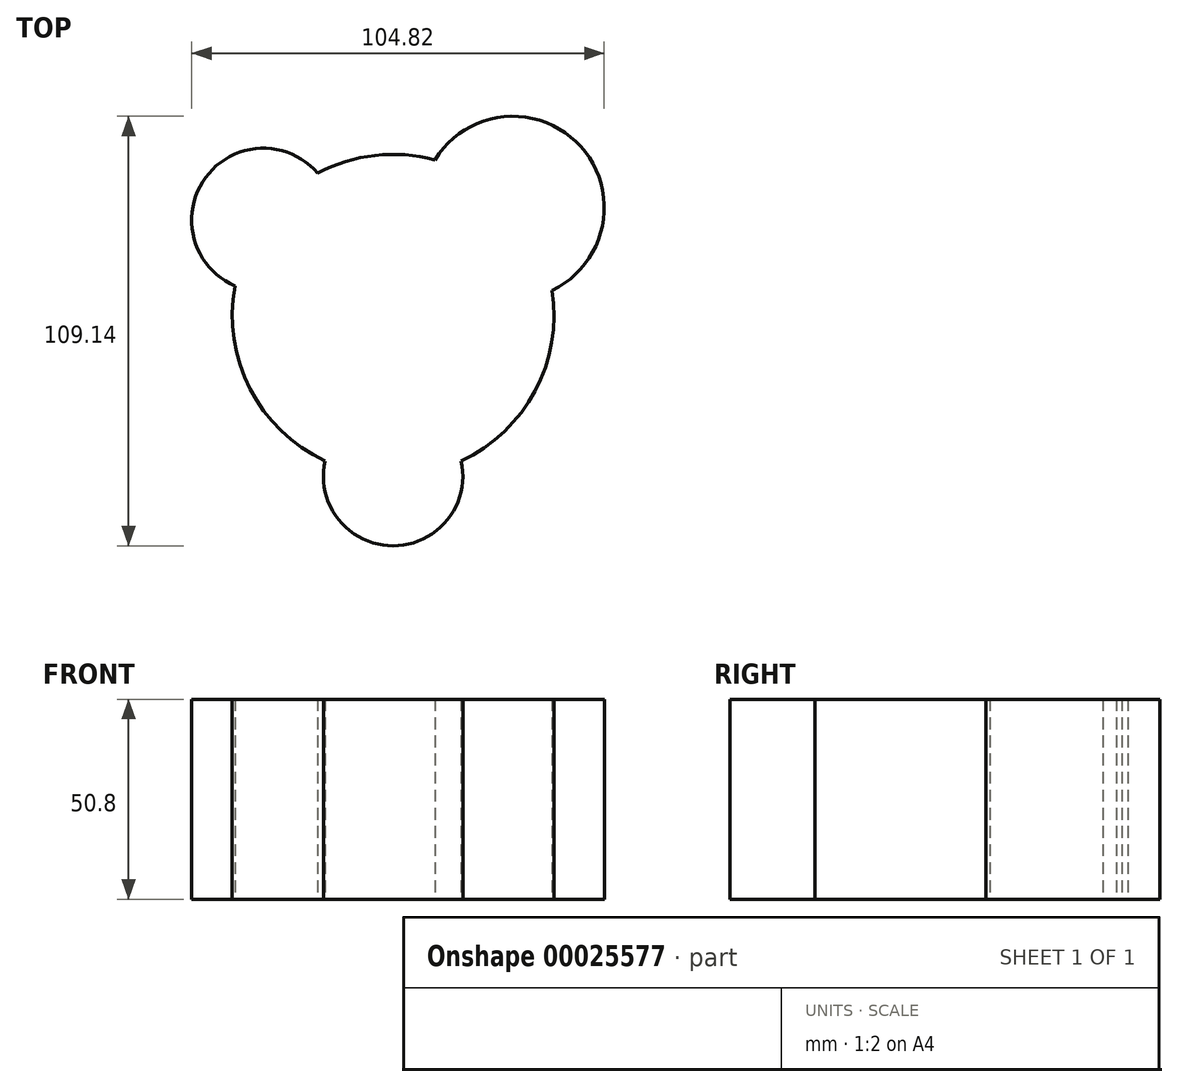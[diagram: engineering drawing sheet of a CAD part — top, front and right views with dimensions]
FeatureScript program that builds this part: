
annotation { "Feature Type Name" : "Feature", "Feature Type Description" : "" }
export const myFeature = defineFeature(function(context is Context, id is Id, definition is map)
    precondition{}
    {
        {
            var Q0;
            Q0=qCreatedBy(makeId("Top.planeOp"),FACE);
            var sketch = newSketch(context, id + "F0", { "sketchPlane" : qUnion([Q0])});
            skArc(sketch, "E0", {"start": v(10.61, 39.47) * mm, "mid": v(-4.59, 40.62) * mm, "end": v(-19.15, 36.11) * mm});
            skArc(sketch, "E1", {"start": v(-19.15, 36.11) * mm, "mid": v(-47.65, 34.98) * mm, "end": v(-40.19, 7.45) * mm});
            skArc(sketch, "E2", {"start": v(40.38, 6.33) * mm, "mid": v(47.7, 42.84) * mm, "end": v(10.61, 39.47) * mm});
            skArc(sketch, "E3", {"start": v(-17.3, -37.04) * mm, "mid": v(0, -58.59) * mm, "end": v(17.3, -37.04) * mm});
            skArc(sketch, "E4.trimOffspring", {"start": v(-40.19, 7.45) * mm, "mid": v(-36.34, -18.7) * mm, "end": v(-17.3, -37.04) * mm});
            skArc(sketch, "E5.trimOffspring", {"start": v(17.3, -37.04) * mm, "mid": v(36.08, -19.21) * mm, "end": v(40.38, 6.33) * mm});
            skSolve(sketch);
        }
        {
            var Q0;
            Q0=makeQuery(id+"F0.imprint","IMPRINT",FACE,{"disambiguationData":[TD([[makeQuery(id+"F0.imprint","IMPRINT",EDGE,{"derivedFrom":sQuery(id+"F0.wireOp",EDGE,"E0")}),1.0]])]});
            extrude(context, id + "F1", {"entities" : qUnion([Q0]), "depth" : 50.8 * mm});
        }
    });
